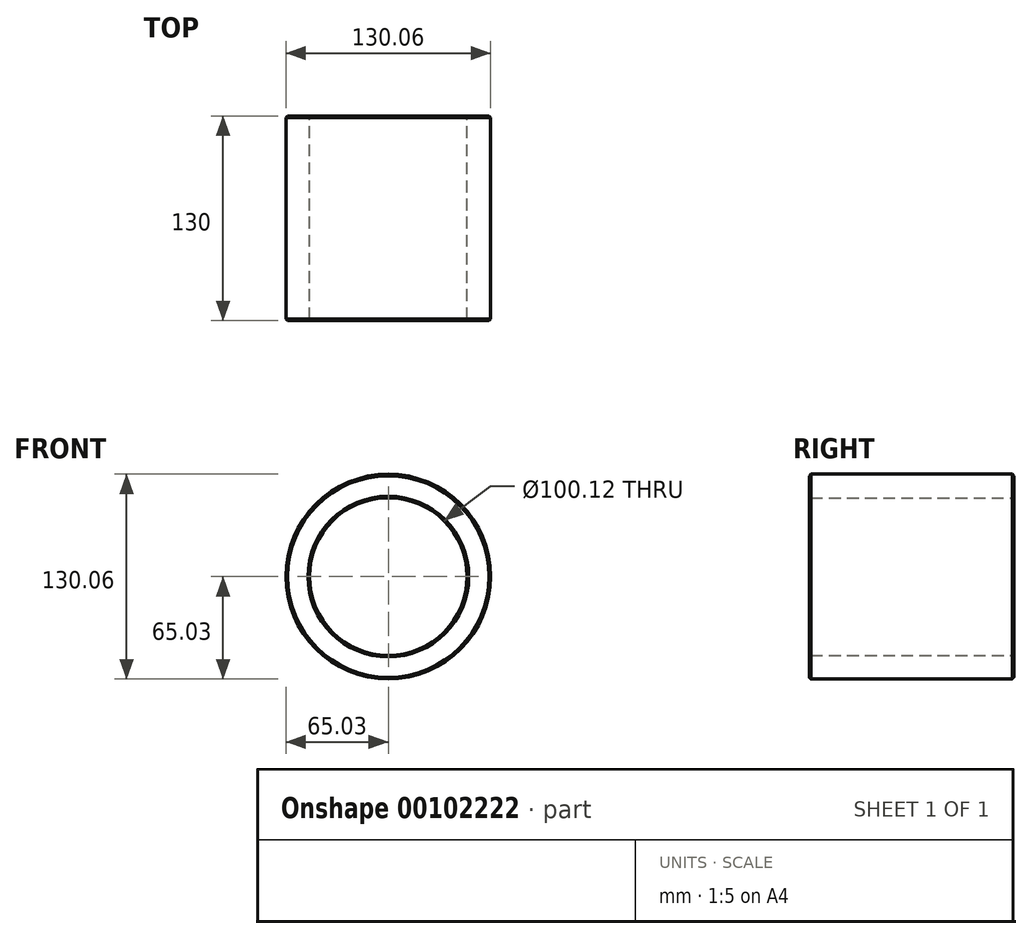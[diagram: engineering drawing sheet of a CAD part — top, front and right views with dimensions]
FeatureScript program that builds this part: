
annotation { "Feature Type Name" : "Feature", "Feature Type Description" : "" }
export const myFeature = defineFeature(function(context is Context, id is Id, definition is map)
    precondition{}
    {
        {
            var Q0;
            Q0=qCreatedBy(makeId("Front.planeOp"),FACE);
            var sketch = newSketch(context, id + "F0", { "sketchPlane" : qUnion([Q0])});
            skCircle(sketch, "E0", {"center": v(0, 0) * mm, "radius": 50.06 * mm});
            skCircle(sketch, "E1", {"center": v(0, 0) * mm, "radius": 65.03 * mm});
            skSolve(sketch);
        }
        {
            var Q0;
            Q0=makeQuery(id+"F0.imprint","IMPRINT",FACE,{"disambiguationData":[TD([[makeQuery(id+"F0.imprint","IMPRINT",EDGE,{"derivedFrom":sQuery(id+"F0.wireOp",EDGE,"E0")}),-1.0]])]});
            extrude(context, id + "F1", {"entities" : qUnion([Q0]), "depth" : 130 * mm});
        }
        {
            var Q0;
            Q0=makeQuery(id+"F1.opExtrude","CAP_EDGE",EDGE,{"disambiguationData":[OSD([sQuery(id+"F0.wireOp",EDGE,"E1")])],"isStart":false});
            var Q1;
            Q1=makeQuery(id+"F1.opExtrude","CAP_EDGE",EDGE,{"disambiguationData":[OSD([sQuery(id+"F0.wireOp",EDGE,"E0")])],"isStart":false});
            var Q2;
            Q2=makeQuery(id+"F1.opExtrude","CAP_EDGE",EDGE,{"disambiguationData":[OSD([sQuery(id+"F0.wireOp",EDGE,"E0")])],"isStart":true});
            var Q3;
            Q3=makeQuery(id+"F1.opExtrude","CAP_EDGE",EDGE,{"disambiguationData":[OSD([sQuery(id+"F0.wireOp",EDGE,"E1")])],"isStart":true});
            chamfer(context, id + "F2", {"entities" : qUnion([Q0, Q1, Q2, Q3]), "width" : 1 * mm, "tangentPropagation" : true});
        }
    });
